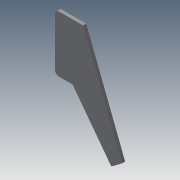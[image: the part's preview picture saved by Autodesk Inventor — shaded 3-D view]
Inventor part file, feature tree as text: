
AUTODESK INVENTOR PART (.ipt)
format: ipt  version: 2013 (Build 170138000, 138)  size: 218,112 bytes
history: native  units: mm
features: sketch x21, extrude x14, fillet x4
ambient origin geometry x8: Origin, YZ Plane, XZ Plane, XY Plane, X Axis, Y Axis, Z Axis, Center Point
bodies: Solid1 (feature_tree)
feature tree (39):
  sketch  "Sketch1"  dims[d4=3.0mm d5=3.0mm d6=2.0mm d7=0.0mm]
  extrude  "Extrusion1"  Depth=2.0mm TaperAngle=0.0deg
  extrude  "Extrusion2"  Depth=2.0mm TaperAngle=0.0deg
  extrude  "Extrusion3"  Depth=2.0mm TaperAngle=0.0deg
  sketch  "Sketch5"  dims[d19=0.5mm d20=0.0mm d21=10.0mm]
  extrude  "Extrusion4"  Depth=6.0mm TaperAngle=0.0deg
  sketch  "Sketch7"  dims[d25=1.5mm d26=0.0mm d27=10.0mm d28=0.0mm]
  sketch  "Sketch8"  dims[d29=2.0mm d30=2.0mm d31=10.0mm d32=0.0mm d33=6.5mm d34=0.0mm]
  extrude  "Extrusion5"  Depth=10.0mm
  sketch  "Sketch10"  dims[d39=2.0mm d43=0.01mm]
  extrude  "Extrusion6"  Depth=1.5mm TaperAngle=0.0deg
  extrude  "Extrusion7"  Depth=10.0mm TaperAngle=0.0deg
  extrude  "Extrusion8"  Depth=2.0mm
  fillet  "Fillet1"  Radius=10.0mm
  fillet  "Fillet2"  Radius=6.5mm
  sketch  "Sketch14"
  extrude  "Extrusion9"  Depth=2.0mm
  extrude  "Extrusion10"  Depth=0.01mm
  sketch  "Sketch17"
  sketch  "Sketch18"
  extrude  "Extrusion11"  Depth=0.2mm
  fillet  "Fillet3"  Radius=0.2mm
  fillet  "Fillet4"  Radius=10.0mm
  extrude  "Extrusion12"  Depth=0.2mm
  extrude  "Extrusion13"  [1 undecoded]
  extrude  "Extrusion14"  [1 undecoded]
  sketch  "Sketch2"  dims[d8=10.0mm d11=2.0mm d12=0.0mm]
  sketch  "Sketch3"  dims[d13=5.0mm d14=2.0mm d15=0.0mm]
  sketch  "Sketch4"  dims[d16=2.0mm d17=6.0mm d18=0.0mm]
  sketch  "Sketch6"  dims[d22=5.0mm d23=1.5mm d24=0.0mm]
  sketch  "Sketch9"  dims[d36=2.0mm d37=0.0mm d38=2.0mm]
  sketch  "Sketch11"  dims[d44=10.0mm d45=0.0mm d46=0.2mm d47=0.2mm d48=10.0mm d49=0.0mm]
  sketch  "Sketch12"  dims[d50=0.2mm d51=0.2mm]
  sketch  "Sketch13"  dims[d52=1.5mm d53=0.0mm]
  sketch  "Sketch15"
  sketch  "Sketch16"
  sketch  "Sketch19"
  sketch  "Sketch20"
  sketch  "Sketch21"
note: 2 required parameter values undecoded (feature->parameter linkage not recoverable at this tier; creation-order binding heuristic only, values carry confidence <= 0.55)
